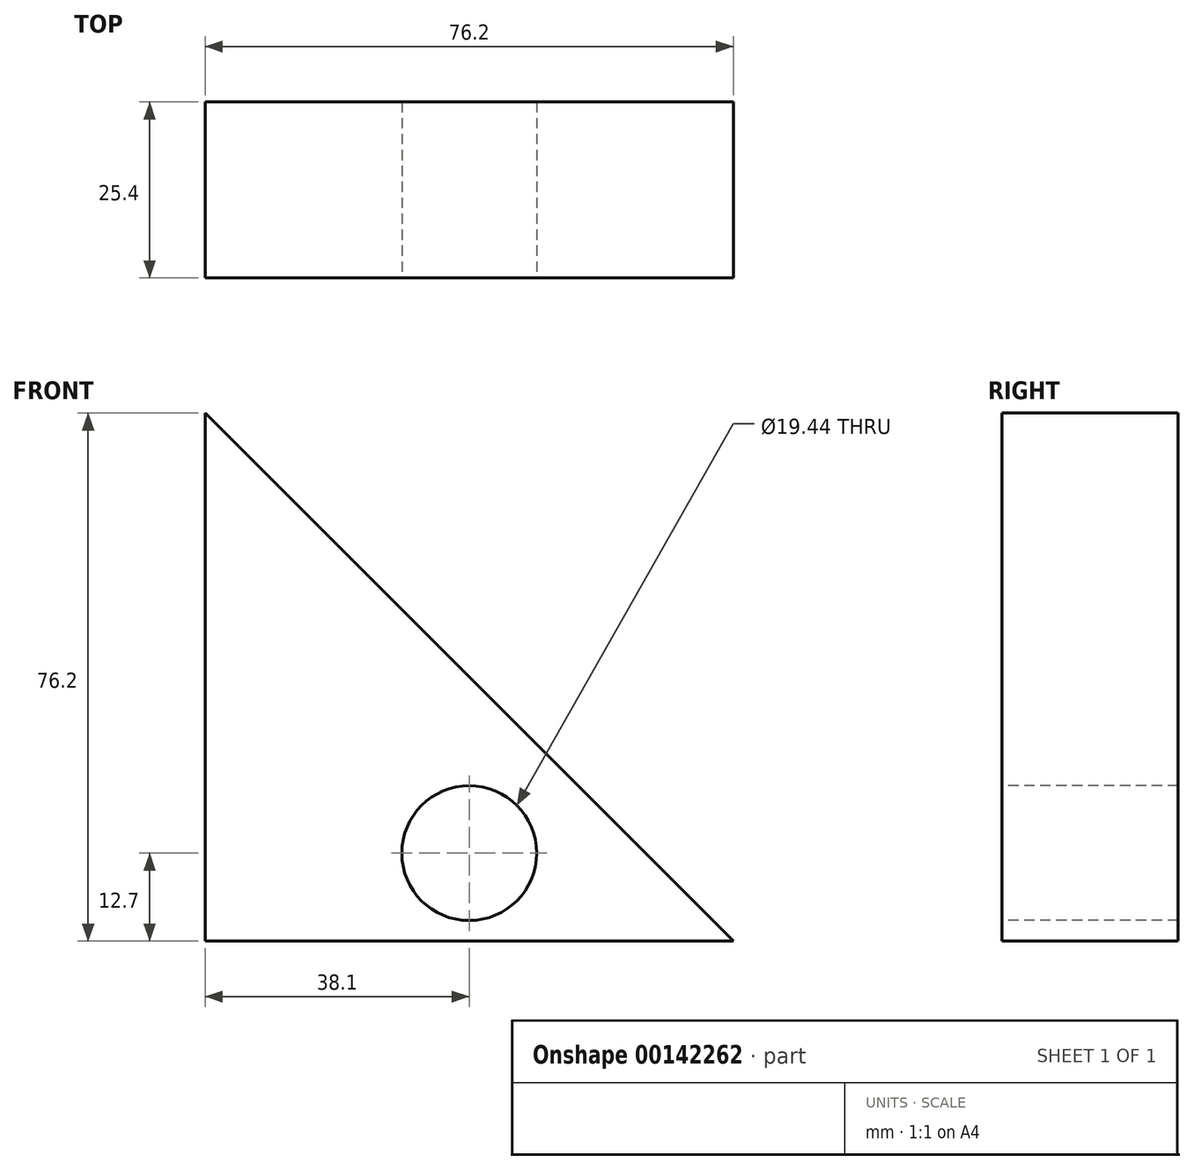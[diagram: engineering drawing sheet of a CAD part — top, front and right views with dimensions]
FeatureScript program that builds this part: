
annotation { "Feature Type Name" : "Feature", "Feature Type Description" : "" }
export const myFeature = defineFeature(function(context is Context, id is Id, definition is map)
    precondition{}
    {
        {
            var Q0;
            Q0=qCreatedBy(makeId("Front.planeOp"),FACE);
            var sketch = newSketch(context, id + "F0", { "sketchPlane" : qUnion([Q0])});
            skLineSegment(sketch, "E0", {"start": v(76.2, 0) * mm, "end": v(0, 0) * mm});
            skLineSegment(sketch, "E1", {"start": v(76.2, 0) * mm, "end": v(0, 76.2) * mm});
            skLineSegment(sketch, "E2", {"start": v(0, 76.2) * mm, "end": v(0, 0) * mm});
            skSolve(sketch);
        }
        {
            var Q0;
            Q0=qSketchRegion(id+"F0",true);
            extrude(context, id + "F1", {"entities" : qUnion([Q0]), "depth" : 25.4 * mm});
        }
        {
            var Q0;
            Q0=makeQuery(id+"F1.opExtrude","CAP_FACE",FACE,{"disambiguationData":[OSD([sQuery(id+"F0.wireOp",EDGE,"E0"),sQuery(id+"F0.wireOp",EDGE,"E1"),sQuery(id+"F0.wireOp",EDGE,"E2")])],"isStart":false});
            var sketch = newSketch(context, id + "F2", { "sketchPlane" : qUnion([Q0])});
            skCircle(sketch, "E3", {"center": v(38.1, 12.7) * mm, "radius": 9.72 * mm});
            skSolve(sketch);
        }
        {
            var Q0;
            Q0=qSketchRegion(id+"F2",true);
            extrude(context, id + "F3", {"entities" : qUnion([Q0]), "operationType" : NewBodyOperationType.REMOVE, "endBound" : BoundingType.THROUGH_ALL, "oppositeDirection" : true, "depth" : 25.4 * mm});
        }
    });
